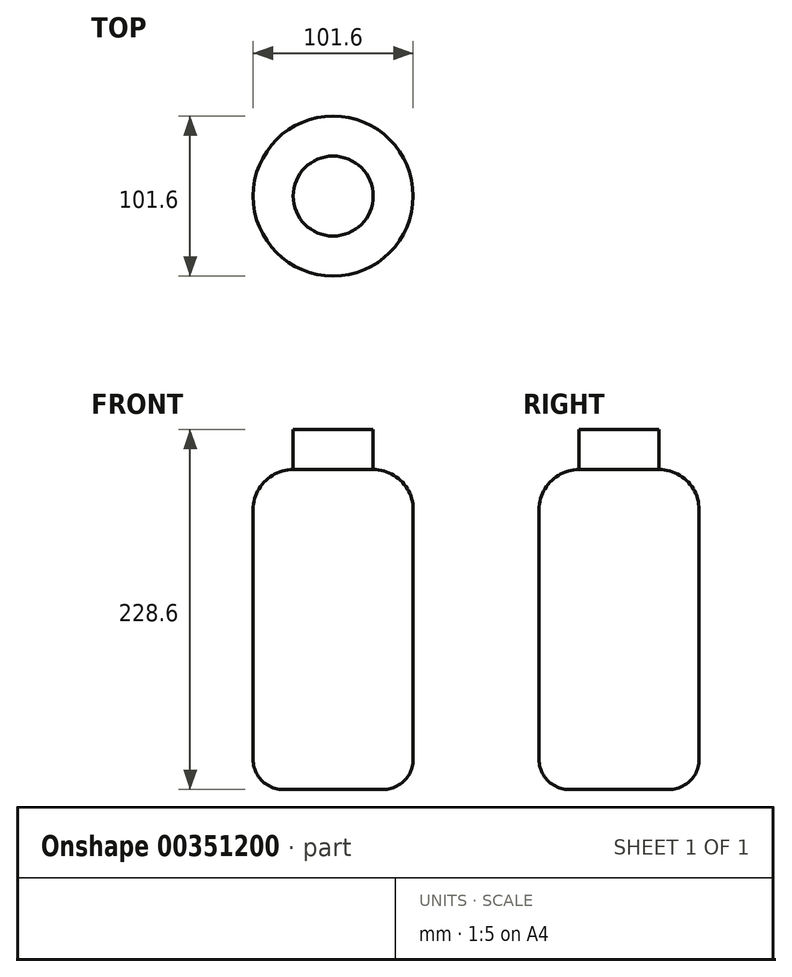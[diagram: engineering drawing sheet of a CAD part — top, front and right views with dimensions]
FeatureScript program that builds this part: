
annotation { "Feature Type Name" : "Feature", "Feature Type Description" : "" }
export const myFeature = defineFeature(function(context is Context, id is Id, definition is map)
    precondition{}
    {
        {
            var Q0;
            Q0=qCreatedBy(makeId("Front.planeOp"),FACE);
            var sketch = newSketch(context, id + "F0", { "sketchPlane" : qUnion([Q0])});
            skLineSegment(sketch, "E0.bottom", {"start": v(-39.72, 138.4) * mm, "end": v(11.08, 138.4) * mm});
            skLineSegment(sketch, "E0.top", {"start": v(-46.07, -64.8) * mm, "end": v(17.43, -64.8) * mm});
            skLineSegment(sketch, "E0.left", {"start": v(-65.12, 113) * mm, "end": v(-65.12, -45.75) * mm});
            skLineSegment(sketch, "E0.right", {"start": v(36.48, 113) * mm, "end": v(36.48, -45.75) * mm});
            skPoint(sketch, "E1.visualSharp", {"position": v(36.48, -64.8) * mm});
            skArc(sketch, "E1.filletArc", {"start": v(17.43, -64.8) * mm, "mid": v(30.9, -59.22) * mm, "end": v(36.48, -45.75) * mm});
            skPoint(sketch, "E2.visualSharp", {"position": v(-65.12, -64.8) * mm});
            skArc(sketch, "E2.filletArc", {"start": v(-65.12, -45.75) * mm, "mid": v(-59.54, -59.22) * mm, "end": v(-46.07, -64.8) * mm});
            skPoint(sketch, "E3.visualSharp", {"position": v(-65.12, 138.4) * mm});
            skArc(sketch, "E3.filletArc", {"start": v(-39.72, 138.4) * mm, "mid": v(-57.68, 130.96) * mm, "end": v(-65.12, 113) * mm});
            skPoint(sketch, "E4.visualSharp", {"position": v(36.48, 138.4) * mm});
            skArc(sketch, "E4.filletArc", {"start": v(36.48, 113) * mm, "mid": v(29.04, 130.96) * mm, "end": v(11.08, 138.4) * mm});
            skLineSegment(sketch, "E5", {"start": v(-14.9, -62.08) * mm, "end": v(-14.32, -64.8) * mm});
            skLineSegment(sketch, "E6", {"start": v(-14.32, 138.4) * mm, "end": v(-14.32, -64.8) * mm});
            skSolve(sketch);
        }
        {
            var Q0;
            Q0=makeQuery(id+"F0.imprint","IMPRINT",FACE,{"disambiguationData":[TD([[makeQuery(id+"F0.imprint","IMPRINT",EDGE,{"derivedFrom":sQuery(id+"F0.wireOp",EDGE,"E0.right")}),-1.0]])]});
            var Q1;
            Q1=sQuery(id+"F0.wireOp",EDGE,"E6");
            revolve(context, id + "F1", {"entities" : qUnion([Q0]), "axis" : qUnion([Q1]), "revolveType" : RevolveType.FULL});
        }
        {
            var Q0;
            Q0=makeQuery(id+"F1.opRevolve","SWEPT_FACE",FACE,{"disambiguationData":[OSD([sQuery(id+"F0.wireOp",EDGE,"E0.bottom")])]});
            var sketch = newSketch(context, id + "F2", { "sketchPlane" : qUnion([Q0])});
            skCircle(sketch, "E7", {"center": v(-14.32, 0) * mm, "radius": 25.4 * mm});
            skSolve(sketch);
        }
        {
            var Q0;
            Q0=makeQuery(id+"F2.imprint","IMPRINT",FACE,{"disambiguationData":[TD([[makeQuery(id+"F2.imprint","IMPRINT",EDGE,{"derivedFrom":sQuery(id+"F2.wireOp",EDGE,"E7")}),1.0]])]});
            extrude(context, id + "F3", {"entities" : qUnion([Q0]), "operationType" : NewBodyOperationType.ADD, "depth" : 25.4 * mm});
        }
    });
